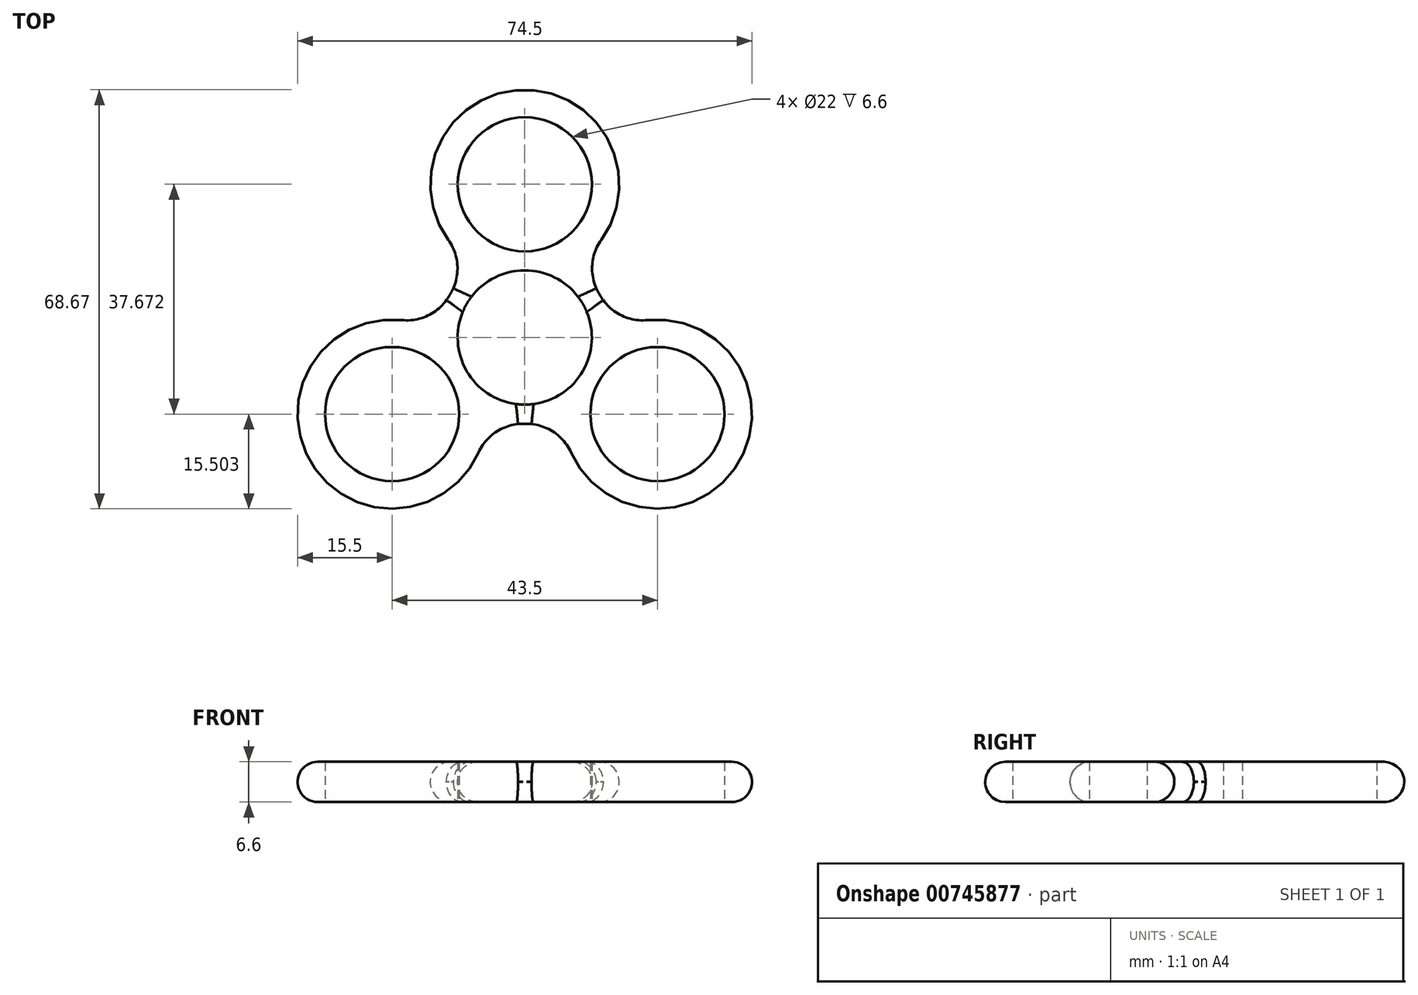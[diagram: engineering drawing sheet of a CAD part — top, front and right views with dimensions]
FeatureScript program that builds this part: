
annotation { "Feature Type Name" : "Feature", "Feature Type Description" : "" }
export const myFeature = defineFeature(function(context is Context, id is Id, definition is map)
    precondition{}
    {
        {
            var Q0;
            Q0=qCreatedBy(makeId("Top.planeOp"),FACE);
            var sketch = newSketch(context, id + "F0", { "sketchPlane" : qUnion([Q0])});
            skCircle(sketch, "E0", {"center": v(0, 25.11) * mm, "radius": 11 * mm});
            skCircle(sketch, "E1", {"center": v(21.75, -12.56) * mm, "radius": 11 * mm});
            skCircle(sketch, "E2", {"center": v(-21.75, -12.56) * mm, "radius": 11 * mm});
            skLineSegment(sketch, "E3", {"start": v(0, 0) * mm, "end": v(0, 25.11) * mm, "construction": true});
            skLineSegment(sketch, "E4", {"start": v(0, 25.11) * mm, "end": v(21.75, -12.56) * mm, "construction": true});
            skLineSegment(sketch, "E5", {"start": v(21.75, -12.56) * mm, "end": v(-21.75, -12.56) * mm, "construction": true});
            skLineSegment(sketch, "E6", {"start": v(-21.75, -12.56) * mm, "end": v(0, 25.11) * mm, "construction": true});
            skLineSegment(sketch, "E7", {"start": v(-21.75, -12.56) * mm, "end": v(0, 0) * mm, "construction": true});
            skLineSegment(sketch, "E8", {"start": v(21.75, -12.56) * mm, "end": v(0, 0) * mm, "construction": true});
            skCircle(sketch, "E9", {"center": v(0, 0) * mm, "radius": 11 * mm});
            skLineSegment(sketch, "E10", {"start": v(0, 14.11) * mm, "end": v(0, 11) * mm, "construction": true});
            skLineSegment(sketch, "E11", {"start": v(0, 11) * mm, "end": v(0, 14.11) * mm, "construction": true});
            skLineSegment(sketch, "E12", {"start": v(0, 12.56) * mm, "end": v(-54.38, 12.56) * mm, "construction": true});
            skLineSegment(sketch, "E13", {"start": v(0, 12.56) * mm, "end": v(2.3, 12.56) * mm, "construction": true});
            skLineSegment(sketch, "E14", {"start": v(60.58, 12.56) * mm, "end": v(0, 12.56) * mm, "construction": true});
            skArc(sketch, "E15", {"start": v(-12.55, 16.02) * mm, "mid": v(0, 40.61) * mm, "end": v(12.55, 16.02) * mm});
            skArc(sketch, "E16.MirrorCS", {"start": v(7.6, -18.88) * mm, "mid": v(35.17, -20.3) * mm, "end": v(20.15, 2.86) * mm});
            skArc(sketch, "E17.MirrorCS", {"start": v(-20.15, 2.86) * mm, "mid": v(-35.17, -20.3) * mm, "end": v(-7.6, -18.88) * mm});
            skLineSegment(sketch, "E18", {"start": v(-12.1, 7.33) * mm, "end": v(-12.4, 6.82) * mm});
            skLineSegment(sketch, "E19", {"start": v(12.1, 7.33) * mm, "end": v(12.4, 6.82) * mm});
            skLineSegment(sketch, "E20", {"start": v(0.3, -14.15) * mm, "end": v(-0.3, -14.15) * mm});
            skPoint(sketch, "E21.visualSharp", {"position": v(9.09, 12.56) * mm});
            skArc(sketch, "E21.filletArc", {"start": v(12.55, 16.02) * mm, "mid": v(11.04, 11.74) * mm, "end": v(12.1, 7.33) * mm});
            skPoint(sketch, "E22.visualSharp", {"position": v(15.42, 1.6) * mm});
            skArc(sketch, "E22.filletArc", {"start": v(12.4, 6.82) * mm, "mid": v(15.7, 3.7) * mm, "end": v(20.15, 2.86) * mm});
            skPoint(sketch, "E23.visualSharp", {"position": v(-9.09, 12.56) * mm});
            skArc(sketch, "E23.filletArc", {"start": v(-12.1, 7.33) * mm, "mid": v(-11.04, 11.74) * mm, "end": v(-12.55, 16.02) * mm});
            skPoint(sketch, "E24.visualSharp", {"position": v(-15.42, 1.6) * mm});
            skArc(sketch, "E24.filletArc", {"start": v(-20.15, 2.86) * mm, "mid": v(-15.7, 3.7) * mm, "end": v(-12.4, 6.82) * mm});
            skPoint(sketch, "E25.visualSharp", {"position": v(-6.33, -14.15) * mm});
            skArc(sketch, "E25.filletArc", {"start": v(-0.3, -14.15) * mm, "mid": v(-4.65, -15.44) * mm, "end": v(-7.6, -18.88) * mm});
            skPoint(sketch, "E26.visualSharp", {"position": v(6.33, -14.15) * mm});
            skArc(sketch, "E26.filletArc", {"start": v(7.6, -18.88) * mm, "mid": v(4.65, -15.44) * mm, "end": v(0.3, -14.15) * mm});
            skSolve(sketch);
        }
        {
            var Q0;
            Q0=makeQuery(id+"F0.imprint","IMPRINT",FACE,{"disambiguationData":[TD([[makeQuery(id+"F0.imprint","IMPRINT",EDGE,{"derivedFrom":sQuery(id+"F0.wireOp",EDGE,"E0")}),-1.0]])]});
            extrude(context, id + "F1", {"entities" : qUnion([Q0]), "depth" : 6.6 * mm, "offsetDistance" : 25 * mm});
        }
        {
            var Q0;
            Q0=makeQuery(id+"F1.opExtrude","CAP_EDGE",EDGE,{"disambiguationData":[OSD([sQuery(id+"F0.wireOp",EDGE,"E21.filletArc")])],"isStart":false});
            var Q1;
            Q1=makeQuery(id+"F1.opExtrude","CAP_EDGE",EDGE,{"disambiguationData":[OSD([sQuery(id+"F0.wireOp",EDGE,"E22.filletArc")])],"isStart":false});
            var Q2;
            Q2=makeQuery(id+"F1.opExtrude","CAP_EDGE",EDGE,{"disambiguationData":[OSD([sQuery(id+"F0.wireOp",EDGE,"E16.MirrorCS")])],"isStart":true});
            var Q3;
            Q3=makeQuery(id+"F1.opExtrude","CAP_EDGE",EDGE,{"disambiguationData":[OSD([sQuery(id+"F0.wireOp",EDGE,"E22.filletArc")])],"isStart":true});
            var Q4;
            Q4=makeQuery(id+"F1.opExtrude","CAP_EDGE",EDGE,{"disambiguationData":[OSD([sQuery(id+"F0.wireOp",EDGE,"E21.filletArc")])],"isStart":true});
            var Q5;
            Q5=makeQuery(id+"F1.opExtrude","CAP_EDGE",EDGE,{"disambiguationData":[OSD([sQuery(id+"F0.wireOp",EDGE,"E15")])],"isStart":true});
            var Q6;
            Q6=makeQuery(id+"F1.opExtrude","CAP_EDGE",EDGE,{"disambiguationData":[OSD([sQuery(id+"F0.wireOp",EDGE,"E23.filletArc")])],"isStart":true});
            var Q7;
            Q7=makeQuery(id+"F1.opExtrude","CAP_EDGE",EDGE,{"disambiguationData":[OSD([sQuery(id+"F0.wireOp",EDGE,"E24.filletArc")])],"isStart":true});
            var Q8;
            Q8=makeQuery(id+"F1.opExtrude","CAP_EDGE",EDGE,{"disambiguationData":[OSD([sQuery(id+"F0.wireOp",EDGE,"E17.MirrorCS")])],"isStart":true});
            var Q9;
            Q9=makeQuery(id+"F1.opExtrude","CAP_EDGE",EDGE,{"disambiguationData":[OSD([sQuery(id+"F0.wireOp",EDGE,"E25.filletArc")])],"isStart":true});
            var Q10;
            Q10=makeQuery(id+"F1.opExtrude","CAP_EDGE",EDGE,{"disambiguationData":[OSD([sQuery(id+"F0.wireOp",EDGE,"E26.filletArc")])],"isStart":true});
            fillet(context, id + "F2", {"entities" : qUnion([Q0, Q1, Q2, Q3, Q4, Q5, Q6, Q7, Q8, Q9, Q10]), "radius" : 3.3 * mm, "tangentPropagation" : true, "allowEdgeOverflow" : false});
        }
    });
